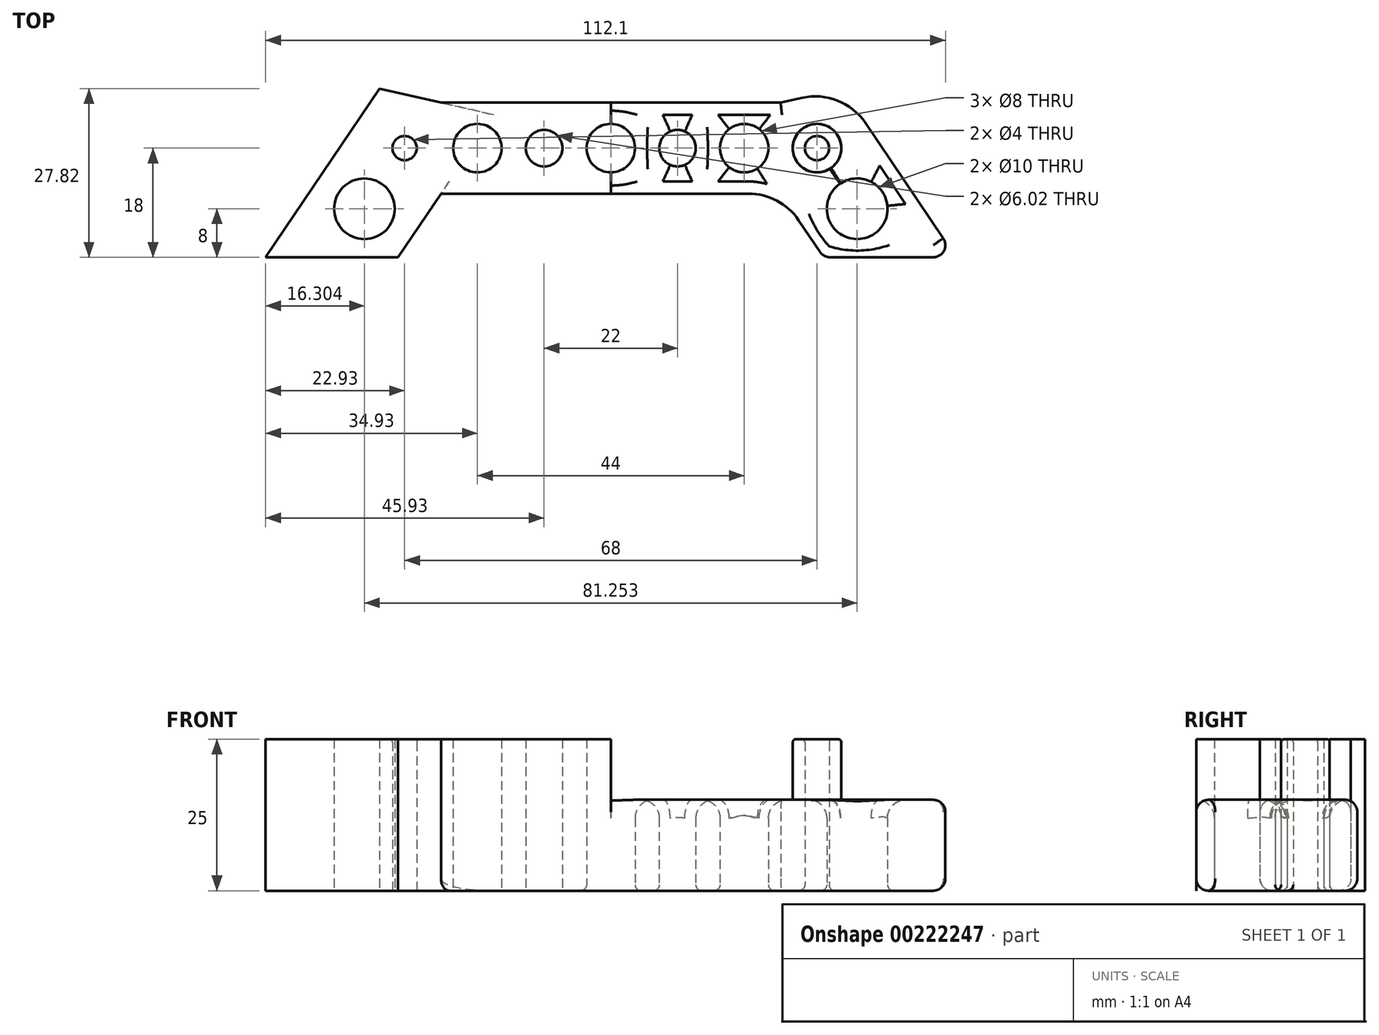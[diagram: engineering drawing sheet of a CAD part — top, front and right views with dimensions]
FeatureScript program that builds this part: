
annotation { "Feature Type Name" : "Feature", "Feature Type Description" : "" }
export const myFeature = defineFeature(function(context is Context, id is Id, definition is map)
    precondition{}
    {
        {
            var Q0;
            Q0=qCreatedBy(makeId("Top.planeOp"),FACE);
            var sketch = newSketch(context, id + "F0", { "sketchPlane" : qUnion([Q0])});
            skLineSegment(sketch, "E0.bottom", {"start": v(0, 0) * mm, "end": v(28, 0) * mm});
            skLineSegment(sketch, "E0.top", {"start": v(0, 15) * mm, "end": v(28, 15) * mm});
            skLineSegment(sketch, "E0.left", {"start": v(0, 0) * mm, "end": v(0, 15) * mm});
            skLineSegment(sketch, "E0.right", {"start": v(28, 0) * mm, "end": v(28, 15) * mm});
            skLineSegment(sketch, "E1", {"start": v(28, 15) * mm, "end": v(38.14, 17.32) * mm});
            skLineSegment(sketch, "E2", {"start": v(38.14, 17.32) * mm, "end": v(56.93, -10.5) * mm});
            skLineSegment(sketch, "E3", {"start": v(56.93, -10.5) * mm, "end": v(35.1, -10.5) * mm});
            skLineSegment(sketch, "E4", {"start": v(35.1, -10.5) * mm, "end": v(28, 0) * mm});
            skCircle(sketch, "E5", {"center": v(34, 7.5) * mm, "radius": 4 * mm});
            skPoint(sketch, "E5.centerSnap0", {"position": v(28, 7.5) * mm});
            skCircle(sketch, "E6", {"center": v(34, 7.5) * mm, "radius": 2 * mm});
            skLineSegment(sketch, "E7.MirrorCS", {"start": v(0, 15) * mm, "end": v(-28, 15) * mm});
            skLineSegment(sketch, "E8.MirrorCS", {"start": v(0, 0) * mm, "end": v(-28, 0) * mm});
            skLineSegment(sketch, "E9.MirrorCS", {"start": v(-35.1, -10.5) * mm, "end": v(-28, 0) * mm});
            skLineSegment(sketch, "E10.MirrorCS", {"start": v(-56.93, -10.5) * mm, "end": v(-35.1, -10.5) * mm});
            skLineSegment(sketch, "E11.MirrorCS", {"start": v(-38.14, 17.32) * mm, "end": v(-56.93, -10.5) * mm});
            skLineSegment(sketch, "E12.MirrorCS", {"start": v(-28, 15) * mm, "end": v(-38.14, 17.32) * mm});
            skCircle(sketch, "E13.MirrorC", {"center": v(-34, 7.5) * mm, "radius": 2 * mm});
            skCircle(sketch, "E14", {"center": v(0, 7.5) * mm, "radius": 4 * mm});
            skCircle(sketch, "E15", {"center": v(11, 7.5) * mm, "radius": 3 * mm});
            skCircle(sketch, "E16", {"center": v(22, 7.5) * mm, "radius": 4 * mm});
            skCircle(sketch, "E17.MirrorC", {"center": v(-22, 7.5) * mm, "radius": 4 * mm});
            skCircle(sketch, "E18.MirrorC", {"center": v(-11, 7.5) * mm, "radius": 3 * mm});
            skCircle(sketch, "E19", {"center": v(40.63, -2.5) * mm, "radius": 5 * mm});
            skCircle(sketch, "E20.MirrorC", {"center": v(-40.63, -2.5) * mm, "radius": 5 * mm});
            skSolve(sketch);
        }
        {
            var Q0;
            Q0=makeQuery(id+"F0.imprint","IMPRINT",FACE,{"disambiguationData":[TD([[makeQuery(id+"F0.imprint","IMPRINT",EDGE,{"derivedFrom":sQuery(id+"F0.wireOp",EDGE,"E13.MirrorC")}),-1.0]])]});
            var Q1;
            Q1=makeQuery(id+"F0.imprint","IMPRINT",FACE,{"disambiguationData":[TD([[makeQuery(id+"F0.imprint","IMPRINT",EDGE,{"derivedFrom":sQuery(id+"F0.wireOp",EDGE,"E5")}),1.0]])]});
            extrude(context, id + "F1", {"entities" : qUnion([Q0, Q1]), "depth" : 25 * mm});
        }
        {
            var Q0;
            Q0=qSketchRegion(id+"F0",true);
            extrude(context, id + "F2", {"entities" : qUnion([Q0]), "operationType" : NewBodyOperationType.ADD, "depth" : 15 * mm});
        }
        {
            var Q0;
            Q0=makeQuery(id+"F2.opExtrude","SWEPT_EDGE",EDGE,{"disambiguationData":[OSD([sQuery(id+"F0.wireOp",EDGE,"E11.MirrorCS"),sQuery(id+"F0.wireOp",EDGE,"E12.MirrorCS")])]});
            var Q1;
            Q1=makeQuery(id+"F2.opExtrude","SWEPT_EDGE",EDGE,{"disambiguationData":[OSD([sQuery(id+"F0.wireOp",EDGE,"E1"),sQuery(id+"F0.wireOp",EDGE,"E2")])]});
            var Q2;
            Q2=makeQuery(id+"F2.opExtrude","SWEPT_EDGE",EDGE,{"disambiguationData":[OSD([sQuery(id+"F0.wireOp",EDGE,"E0.bottom"),sQuery(id+"F0.wireOp",EDGE,"E0.right"),sQuery(id+"F0.wireOp",EDGE,"E4")])]});
            var Q3;
            Q3=makeQuery(id+"F2.opExtrude","SWEPT_EDGE",EDGE,{"disambiguationData":[OSD([sQuery(id+"F0.wireOp",EDGE,"E8.MirrorCS"),sQuery(id+"F0.wireOp",EDGE,"E9.MirrorCS")])]});
            fillet(context, id + "F3", {"entities" : qUnion([Q0, Q1, Q2, Q3]), "radius" : 10 * mm, "tangentPropagation" : true, "allowEdgeOverflow" : false});
        }
        {
            var Q0;
            Q0=makeQuery(id+"F2.opExtrude","CAP_EDGE",EDGE,{"disambiguationData":[OSD([sQuery(id+"F0.wireOp",EDGE,"E13.MirrorC")])],"isStart":false});
            var Q1;
            Q1=makeQuery(id+"F2.opExtrude","CAP_EDGE",EDGE,{"disambiguationData":[OSD([sQuery(id+"F0.wireOp",EDGE,"E5")])],"isStart":false});
            var Q2;
            Q2=makeQuery(id+"F1.opExtrude","CAP_EDGE",EDGE,{"disambiguationData":[OSD([sQuery(id+"F0.wireOp",EDGE,"E13.MirrorC")])],"isStart":false});
            var Q3;
            Q3=makeQuery(id+"F1.opExtrude","CAP_EDGE",EDGE,{"disambiguationData":[OSD([sQuery(id+"F0.wireOp",EDGE,"E5")])],"isStart":false});
            var Q4;
            Q4=makeQuery(id+"F1.opExtrude","CAP_EDGE",EDGE,{"disambiguationData":[OSD([sQuery(id+"F0.wireOp",EDGE,"E6")])],"isStart":false});
            fillet(context, id + "F4", {"entities" : qUnion([Q0, Q1, Q2, Q3, Q4]), "radius" : 0.5 * mm, "tangentPropagation" : true, "allowEdgeOverflow" : false});
        }
        {
            var Q0;
            Q0=makeQuery(id+"F2.opExtrude","CAP_EDGE",EDGE,{"disambiguationData":[OSD([sQuery(id+"F0.wireOp",EDGE,"E2")])],"isStart":false});
            var Q1;
            Q1=makeQuery(id+"F2.opExtrude","CAP_EDGE",EDGE,{"disambiguationData":[OSD([sQuery(id+"F0.wireOp",EDGE,"E2")])],"isStart":true});
            var Q2;
            Q2=makeQuery(id+"F2.opExtrude","CAP_EDGE",EDGE,{"disambiguationData":[OSD([sQuery(id+"F0.wireOp",EDGE,"E0.top"),sQuery(id+"F0.wireOp",EDGE,"E1"),sQuery(id+"F0.wireOp",EDGE,"E7.MirrorCS"),sQuery(id+"F0.wireOp",EDGE,"E12.MirrorCS")])],"isStart":false});
            var Q3;
            Q3=makeQuery(id+"F2.opExtrude","CAP_EDGE",EDGE,{"disambiguationData":[OSD([sQuery(id+"F0.wireOp",EDGE,"E0.top"),sQuery(id+"F0.wireOp",EDGE,"E1"),sQuery(id+"F0.wireOp",EDGE,"E7.MirrorCS"),sQuery(id+"F0.wireOp",EDGE,"E12.MirrorCS")])],"isStart":true});
            var Q4;
            Q4=makeQuery(id+"F2.opExtrude","CAP_EDGE",EDGE,{"disambiguationData":[OSD([sQuery(id+"F0.wireOp",EDGE,"E11.MirrorCS")])],"isStart":true});
            var Q5;
            Q5=makeQuery(id+"F2.opExtrude","CAP_EDGE",EDGE,{"disambiguationData":[OSD([sQuery(id+"F0.wireOp",EDGE,"E11.MirrorCS")])],"isStart":false});
            fillet(context, id + "F5", {"entities" : qUnion([Q0, Q1, Q2, Q3, Q4, Q5]), "radius" : 2 * mm, "tangentPropagation" : true, "allowEdgeOverflow" : false});
        }
        {
            var Q0;
            Q0=makeQuery(id+"F2.opExtrude","SWEPT_EDGE",EDGE,{"disambiguationData":[OSD([sQuery(id+"F0.wireOp",EDGE,"E9.MirrorCS"),sQuery(id+"F0.wireOp",EDGE,"E10.MirrorCS")])]});
            var Q1;
            Q1=makeQuery(id+"F2.opExtrude","SWEPT_EDGE",EDGE,{"disambiguationData":[OSD([sQuery(id+"F0.wireOp",EDGE,"E3"),sQuery(id+"F0.wireOp",EDGE,"E4")])]});
            var Q2;
            Q2=makeQuery(id+"F2.opExtrude","SWEPT_EDGE",EDGE,{"disambiguationData":[OSD([sQuery(id+"F0.wireOp",EDGE,"E2"),sQuery(id+"F0.wireOp",EDGE,"E3")])]});
            var Q3;
            Q3=makeQuery(id+"F2.opExtrude","SWEPT_EDGE",EDGE,{"disambiguationData":[OSD([sQuery(id+"F0.wireOp",EDGE,"E10.MirrorCS"),sQuery(id+"F0.wireOp",EDGE,"E11.MirrorCS")])]});
            fillet(context, id + "F6", {"entities" : qUnion([Q0, Q1, Q2, Q3]), "radius" : 2 * mm, "tangentPropagation" : true, "allowEdgeOverflow" : false});
        }
        {
            var Q0;
            Q0=makeQuery(id+"F2.opExtrude","CAP_EDGE",EDGE,{"disambiguationData":[OSD([sQuery(id+"F0.wireOp",EDGE,"E0.bottom"),sQuery(id+"F0.wireOp",EDGE,"E8.MirrorCS")])],"isStart":false});
            var Q1;
            Q1=makeQuery(id+"F2.opExtrude","CAP_EDGE",EDGE,{"disambiguationData":[OSD([sQuery(id+"F0.wireOp",EDGE,"E0.bottom"),sQuery(id+"F0.wireOp",EDGE,"E8.MirrorCS")])],"isStart":true});
            fillet(context, id + "F7", {"entities" : qUnion([Q0, Q1]), "radius" : 2 * mm, "tangentPropagation" : true, "allowEdgeOverflow" : false});
        }
        {
            var Q0;
            Q0=makeQuery(id+"F2.opExtrude","CAP_EDGE",EDGE,{"disambiguationData":[OSD([sQuery(id+"F0.wireOp",EDGE,"E17.MirrorC")])],"isStart":false});
            var Q1;
            Q1=makeQuery(id+"F2.opExtrude","CAP_EDGE",EDGE,{"disambiguationData":[OSD([sQuery(id+"F0.wireOp",EDGE,"E18.MirrorC")])],"isStart":false});
            var Q2;
            Q2=makeQuery(id+"F2.opExtrude","CAP_EDGE",EDGE,{"disambiguationData":[OSD([sQuery(id+"F0.wireOp",EDGE,"E14")])],"isStart":false});
            var Q3;
            Q3=makeQuery(id+"F2.opExtrude","CAP_EDGE",EDGE,{"disambiguationData":[OSD([sQuery(id+"F0.wireOp",EDGE,"E15")])],"isStart":false});
            var Q4;
            Q4=makeQuery(id+"F2.opExtrude","CAP_EDGE",EDGE,{"disambiguationData":[OSD([sQuery(id+"F0.wireOp",EDGE,"E16")])],"isStart":false});
            var Q5;
            Q5=makeQuery(id+"F2.opExtrude","CAP_EDGE",EDGE,{"disambiguationData":[OSD([sQuery(id+"F0.wireOp",EDGE,"E19")])],"isStart":false});
            var Q6;
            Q6=makeQuery(id+"F2.opExtrude","CAP_EDGE",EDGE,{"disambiguationData":[OSD([sQuery(id+"F0.wireOp",EDGE,"E20.MirrorC")])],"isStart":false});
            fillet(context, id + "F8", {"entities" : qUnion([Q0, Q1, Q2, Q3, Q4, Q5, Q6]), "radius" : 3 * mm, "tangentPropagation" : true, "allowEdgeOverflow" : false});
        }
        {
            var Q0;
            Q0=makeQuery(id+"F2.opExtrude","CAP_EDGE",EDGE,{"disambiguationData":[OSD([sQuery(id+"F0.wireOp",EDGE,"E19")])],"isStart":true});
            var Q1;
            Q1=makeQuery(id+"F1.opExtrude","CAP_EDGE",EDGE,{"disambiguationData":[OSD([sQuery(id+"F0.wireOp",EDGE,"E6")])],"isStart":true});
            var Q2;
            Q2=makeQuery(id+"F2.opExtrude","CAP_EDGE",EDGE,{"disambiguationData":[OSD([sQuery(id+"F0.wireOp",EDGE,"E16")])],"isStart":true});
            var Q3;
            Q3=makeQuery(id+"F2.opExtrude","CAP_EDGE",EDGE,{"disambiguationData":[OSD([sQuery(id+"F0.wireOp",EDGE,"E15")])],"isStart":true});
            var Q4;
            Q4=makeQuery(id+"F2.opExtrude","CAP_EDGE",EDGE,{"disambiguationData":[OSD([sQuery(id+"F0.wireOp",EDGE,"E14")])],"isStart":true});
            var Q5;
            Q5=makeQuery(id+"F2.opExtrude","CAP_EDGE",EDGE,{"disambiguationData":[OSD([sQuery(id+"F0.wireOp",EDGE,"E18.MirrorC")])],"isStart":true});
            var Q6;
            Q6=makeQuery(id+"F2.opExtrude","CAP_EDGE",EDGE,{"disambiguationData":[OSD([sQuery(id+"F0.wireOp",EDGE,"E17.MirrorC")])],"isStart":true});
            var Q7;
            Q7=makeQuery(id+"F2.opExtrude","CAP_EDGE",EDGE,{"disambiguationData":[OSD([sQuery(id+"F0.wireOp",EDGE,"E20.MirrorC")])],"isStart":true});
            fillet(context, id + "F9", {"entities" : qUnion([Q0, Q1, Q2, Q3, Q4, Q5, Q6, Q7]), "radius" : 1 * mm, "tangentPropagation" : true, "allowEdgeOverflow" : false});
        }
    });
